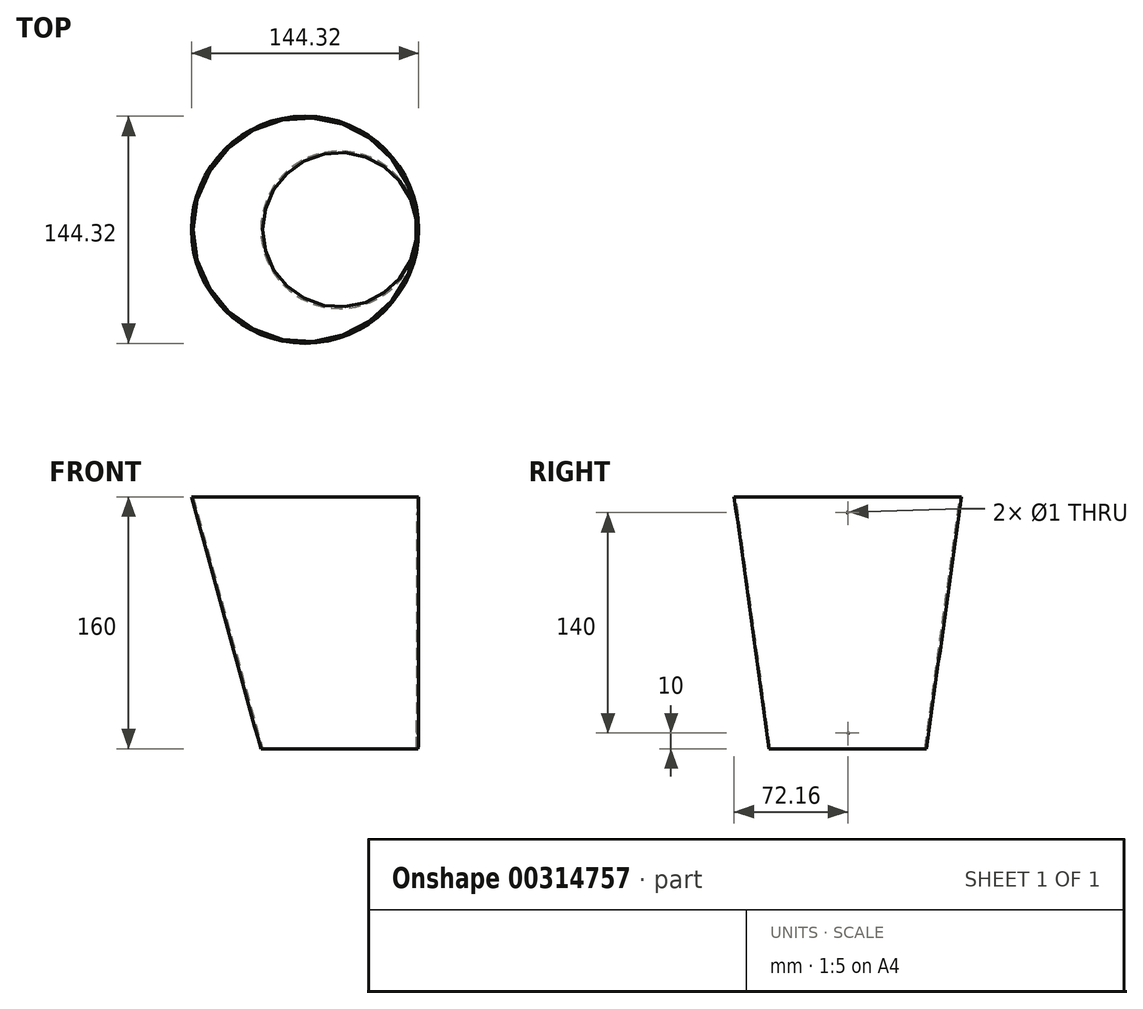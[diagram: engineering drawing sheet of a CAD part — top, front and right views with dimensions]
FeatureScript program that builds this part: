
annotation { "Feature Type Name" : "Feature", "Feature Type Description" : "" }
export const myFeature = defineFeature(function(context is Context, id is Id, definition is map)
    precondition{}
    {
        {
            var Q0;
            Q0=qCreatedBy(makeId("Top.planeOp"),FACE);
            var sketch = newSketch(context, id + "F0", { "sketchPlane" : qUnion([Q0])});
            skCircle(sketch, "E0", {"center": v(0, 0) * mm, "radius": 50 * mm});
            skSolve(sketch);
        }
        {
            var Q0;
            Q0=makeQuery(id+"F0.imprint","IMPRINT",FACE,{"disambiguationData":[TD([[makeQuery(id+"F0.imprint","IMPRINT",EDGE,{"derivedFrom":sQuery(id+"F0.wireOp",EDGE,"E0")}),1.0]])]});
            cPlane(context, id + "F1", {"entities" : qUnion([Q0]), "cplaneType" : CPlaneType.OFFSET, "offset" : 160 * mm, "width" : 150 * mm, "height" : 150 * mm});
        }
        {
            var Q0;
            Q0=qCreatedBy(id+"F1.planeOp",FACE);
            var sketch = newSketch(context, id + "F2", { "sketchPlane" : qUnion([Q0])});
            skCircle(sketch, "E1", {"center": v(-21.93, 0) * mm, "radius": 72.16 * mm});
            skSolve(sketch);
        }
        {
            var Q0;
            Q0=makeQuery(id+"F2.imprint","IMPRINT",FACE,{"disambiguationData":[TD([[makeQuery(id+"F2.imprint","IMPRINT",EDGE,{"derivedFrom":sQuery(id+"F2.wireOp",EDGE,"E1")}),1.0]])]});
            var Q1;
            Q1=makeQuery(id+"F0.imprint","IMPRINT",FACE,{"disambiguationData":[TD([[makeQuery(id+"F0.imprint","IMPRINT",EDGE,{"derivedFrom":sQuery(id+"F0.wireOp",EDGE,"E0")}),1.0]])]});
            loft(context, id + "F3", {"sheetProfilesArray" : [{ "sheetProfileEntities" : qUnion([Q0]) }, { "sheetProfileEntities" : qUnion([Q1]) }]});
        }
        {
            var Q0;
            Q0=makeQuery(id+"F3.opLoft","CAP_FACE",FACE,{"disambiguationData":[OSD([makeQuery(id+"F0.imprint","IMPRINT",FACE,{"disambiguationData":[TD([[makeQuery(id+"F0.imprint","IMPRINT",EDGE,{"derivedFrom":sQuery(id+"F0.wireOp",EDGE,"E0")}),1.0]])]})])],"isStart":true});
            var Q1;
            Q1=makeQuery(id+"F3.opLoft","CAP_FACE",FACE,{"disambiguationData":[OSD([makeQuery(id+"F2.imprint","IMPRINT",FACE,{"disambiguationData":[TD([[makeQuery(id+"F2.imprint","IMPRINT",EDGE,{"derivedFrom":sQuery(id+"F2.wireOp",EDGE,"E1")}),1.0]])]})])],"isStart":true});
            shell(context, id + "F4", {"entities" : qUnion([Q0, Q1]), "thickness" : 1 * mm});
        }
        {
            var Q0;
            Q0=qCreatedBy(makeId("Right.planeOp"),FACE);
            var sketch = newSketch(context, id + "F5", { "sketchPlane" : qUnion([Q0])});
            skCircle(sketch, "E2", {"center": v(0, 10) * mm, "radius": 1.5 * mm});
            skPoint(sketch, "E3.orphan", {"position": v(0, 158.04) * mm});
            skCircle(sketch, "E4", {"center": v(0, 150) * mm, "radius": 1.5 * mm});
            skSolve(sketch);
        }
        {
            var Q0;
            Q0=qCreatedBy(makeId("Right.planeOp"),FACE);
            var sketch = newSketch(context, id + "F6", { "sketchPlane" : qUnion([Q0])});
            skCircle(sketch, "E5", {"center": v(0, 10) * mm, "radius": 1.5 * mm});
            skCircle(sketch, "E6", {"center": v(0, 150) * mm, "radius": 1.5 * mm});
            skSolve(sketch);
        }
        {
            var Q0;
            Q0=sQuery(id+"F5.wireOp",VERTEX,"E2.center");
            var Q1;
            Q1=makeQuery(id+"F3.opLoft","SWEPT_BODY",BODY,{"disambiguationData":[OSD([makeQuery(id+"F0.imprint","IMPRINT",FACE,{"disambiguationData":[TD([[makeQuery(id+"F0.imprint","IMPRINT",EDGE,{"derivedFrom":sQuery(id+"F0.wireOp",EDGE,"E0")}),1.0]])]}),makeQuery(id+"F2.imprint","IMPRINT",FACE,{"disambiguationData":[TD([[makeQuery(id+"F2.imprint","IMPRINT",EDGE,{"derivedFrom":sQuery(id+"F2.wireOp",EDGE,"E1")}),1.0]])]})])]});
            hole(context, id + "F7", {"style" : HoleStyle.SIMPLE, "endStyle" : HoleEndStyle.THROUGH, "oppositeDirection" : true, "holeDiameter" : 1 * mm, "isTappedThrough" : true, "tappedDepth" : 12 * mm, "tapClearance" : 3, "locations" : qUnion([Q0]), "scope" : qUnion([Q1])});
        }
        {
            var Q0;
            Q0=sQuery(id+"F6.wireOp",VERTEX,"E6.center");
            var Q1;
            Q1=makeQuery(id+"F3.opLoft","SWEPT_BODY",BODY,{"disambiguationData":[OSD([makeQuery(id+"F0.imprint","IMPRINT",FACE,{"disambiguationData":[TD([[makeQuery(id+"F0.imprint","IMPRINT",EDGE,{"derivedFrom":sQuery(id+"F0.wireOp",EDGE,"E0")}),1.0]])]}),makeQuery(id+"F2.imprint","IMPRINT",FACE,{"disambiguationData":[TD([[makeQuery(id+"F2.imprint","IMPRINT",EDGE,{"derivedFrom":sQuery(id+"F2.wireOp",EDGE,"E1")}),1.0]])]})])]});
            hole(context, id + "F8", {"style" : HoleStyle.SIMPLE, "endStyle" : HoleEndStyle.THROUGH, "oppositeDirection" : true, "holeDiameter" : 1 * mm, "isTappedThrough" : true, "tappedDepth" : 12 * mm, "tapClearance" : 3, "locations" : qUnion([Q0]), "scope" : qUnion([Q1])});
        }
    });
